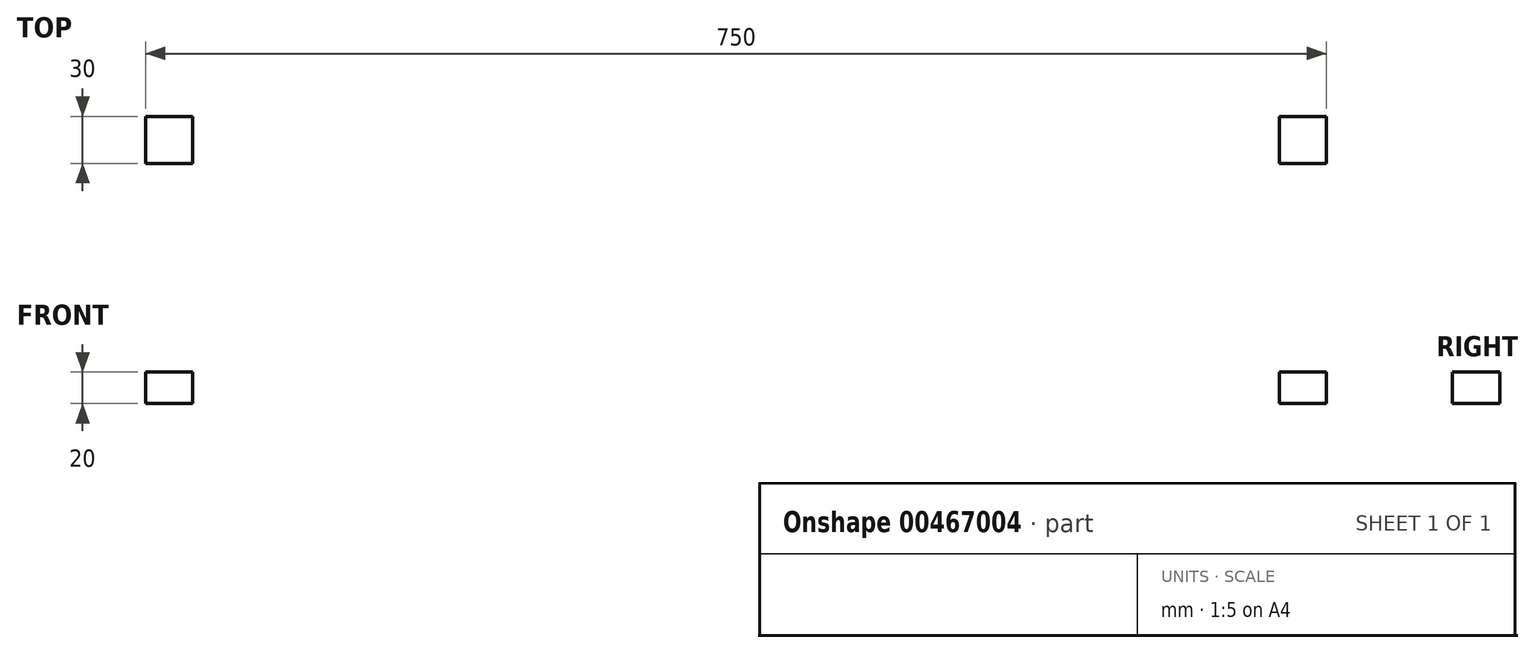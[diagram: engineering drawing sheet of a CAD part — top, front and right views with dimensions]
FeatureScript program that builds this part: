
annotation { "Feature Type Name" : "Feature", "Feature Type Description" : "" }
export const myFeature = defineFeature(function(context is Context, id is Id, definition is map)
    precondition{}
    {
        {
            var Q0;
            Q0=qCreatedBy(makeId("Top.planeOp"),FACE);
            var sketch = newSketch(context, id + "F0", { "sketchPlane" : qUnion([Q0])});
            skLineSegment(sketch, "E0.bottom", {"start": v(0, 0) * mm, "end": v(-750, 0) * mm});
            skLineSegment(sketch, "E0.top", {"start": v(0, -800) * mm, "end": v(-750, -800) * mm});
            skLineSegment(sketch, "E0.left", {"start": v(0, 0) * mm, "end": v(0, -800) * mm});
            skLineSegment(sketch, "E0.right", {"start": v(-750, 0) * mm, "end": v(-750, -800) * mm});
            skLineSegment(sketch, "E1.bottom", {"start": v(-750, 0) * mm, "end": v(-720, 0) * mm});
            skLineSegment(sketch, "E1.top", {"start": v(-750, -30) * mm, "end": v(-720, -30) * mm});
            skLineSegment(sketch, "E1.left", {"start": v(-750, 0) * mm, "end": v(-750, -30) * mm});
            skLineSegment(sketch, "E1.right", {"start": v(-720, 0) * mm, "end": v(-720, -30) * mm});
            skLineSegment(sketch, "E2.bottom", {"start": v(0, 0) * mm, "end": v(-30, 0) * mm});
            skLineSegment(sketch, "E2.top", {"start": v(0, -30) * mm, "end": v(-30, -30) * mm});
            skLineSegment(sketch, "E2.left", {"start": v(0, 0) * mm, "end": v(0, -30) * mm});
            skLineSegment(sketch, "E2.right", {"start": v(-30, 0) * mm, "end": v(-30, -30) * mm});
            skLineSegment(sketch, "E3.bottom", {"start": v(0, -800) * mm, "end": v(-30, -800) * mm});
            skLineSegment(sketch, "E3.top", {"start": v(0, -770) * mm, "end": v(-30, -770) * mm});
            skLineSegment(sketch, "E3.left", {"start": v(0, -800) * mm, "end": v(0, -770) * mm});
            skLineSegment(sketch, "E3.right", {"start": v(-30, -800) * mm, "end": v(-30, -770) * mm});
            skLineSegment(sketch, "E4.bottom", {"start": v(-750, -800) * mm, "end": v(-720, -800) * mm});
            skLineSegment(sketch, "E4.top", {"start": v(-750, -770) * mm, "end": v(-720, -770) * mm});
            skLineSegment(sketch, "E4.left", {"start": v(-750, -800) * mm, "end": v(-750, -770) * mm});
            skLineSegment(sketch, "E4.right", {"start": v(-720, -800) * mm, "end": v(-720, -770) * mm});
            skSolve(sketch);
        }
        {
            var Q0;
            Q0=makeQuery(id+"F0.imprint","IMPRINT",FACE,{"disambiguationData":[TD([[makeQuery(id+"F0.imprint","IMPRINT",EDGE,{"derivedFrom":sQuery(id+"F0.wireOp",EDGE,"E0.bottom")}),1.0]])]});
            extrude(context, id + "F1", {"entities" : qUnion([Q0]), "depth" : 20 * mm, "offsetDistance" : 25 * mm});
        }
    });
